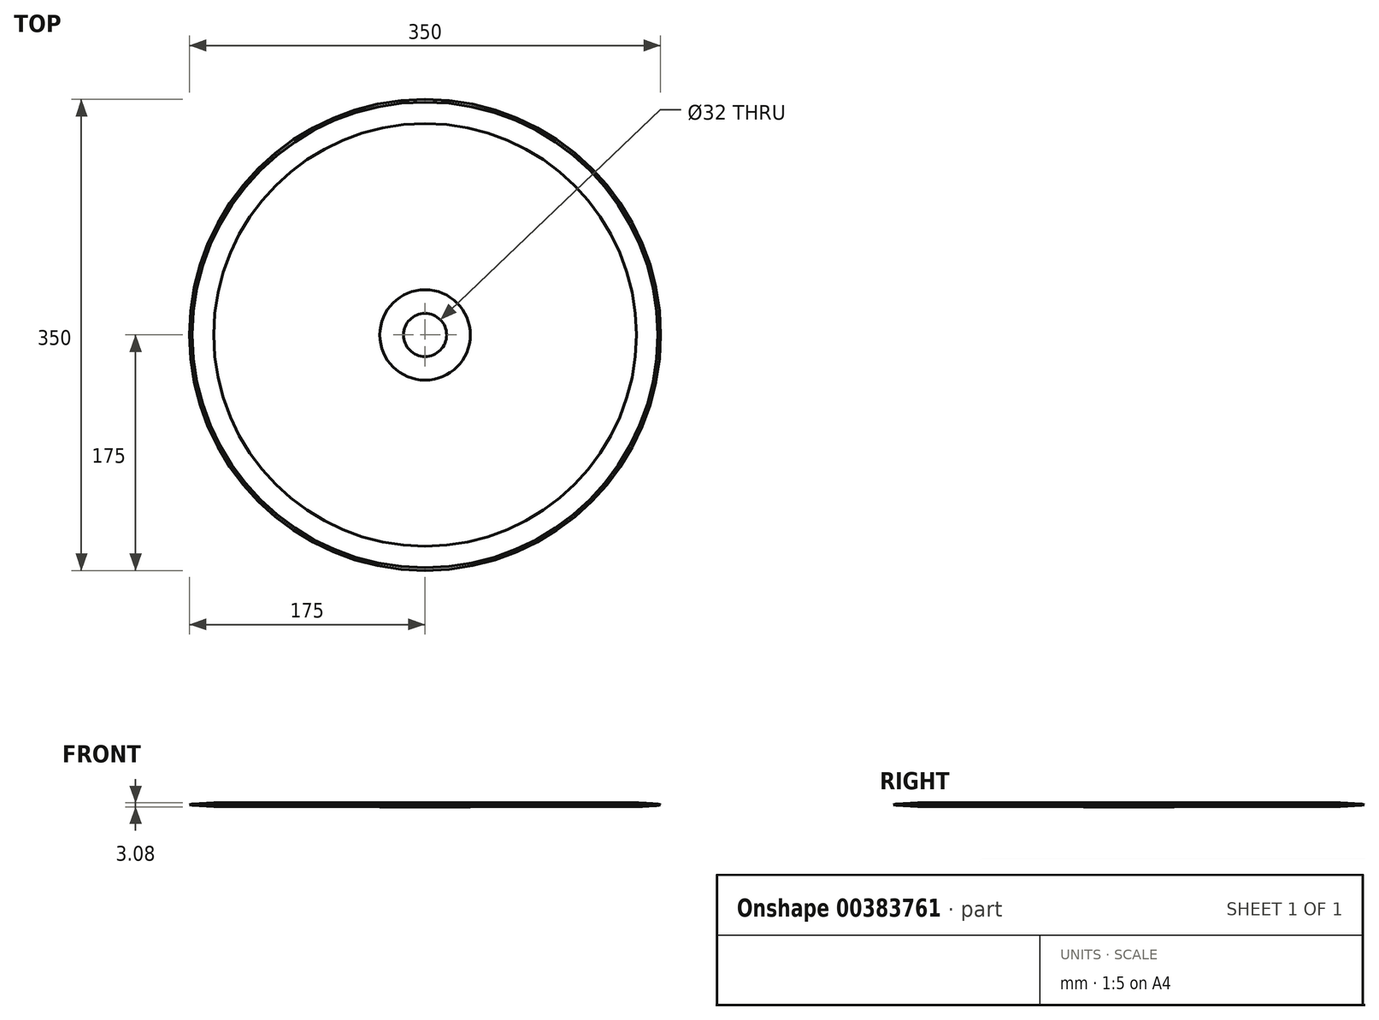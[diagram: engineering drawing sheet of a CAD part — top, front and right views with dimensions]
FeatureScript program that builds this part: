
annotation { "Feature Type Name" : "Feature", "Feature Type Description" : "" }
export const myFeature = defineFeature(function(context is Context, id is Id, definition is map)
    precondition{}
    {
        {
            var Q0;
            Q0=qCreatedBy(makeId("Front.planeOp"),FACE);
            var sketch = newSketch(context, id + "F0", { "sketchPlane" : qUnion([Q0])});
            skLineSegment(sketch, "E0", {"start": v(16, 1.54) * mm, "end": v(33.6, 1.54) * mm});
            skLineSegment(sketch, "E1", {"start": v(33.6, 1.54) * mm, "end": v(33.6, 1.45) * mm});
            skLineSegment(sketch, "E2", {"start": v(16, 1.54) * mm, "end": v(16, 0) * mm});
            skLineSegment(sketch, "E3", {"start": v(33.6, 1.45) * mm, "end": v(157, 1.45) * mm});
            skLineSegment(sketch, "E4", {"start": v(173, 0.5) * mm, "end": v(157, 1.45) * mm});
            skLineSegment(sketch, "E5", {"start": v(175, 0) * mm, "end": v(173, 0.5) * mm});
            skLineSegment(sketch, "E6", {"start": v(0, 0) * mm, "end": v(175, 0) * mm, "construction": true});
            skLineSegment(sketch, "E7.MirrorCS", {"start": v(33.6, -1.54) * mm, "end": v(33.6, -1.45) * mm});
            skLineSegment(sketch, "E8.MirrorCS", {"start": v(175, 0) * mm, "end": v(173, -0.5) * mm});
            skLineSegment(sketch, "E9.MirrorCS", {"start": v(16, -1.54) * mm, "end": v(16, 0) * mm});
            skLineSegment(sketch, "E10.MirrorCS", {"start": v(16, -1.54) * mm, "end": v(33.6, -1.54) * mm});
            skLineSegment(sketch, "E11.MirrorCS", {"start": v(173, -0.5) * mm, "end": v(157, -1.45) * mm});
            skLineSegment(sketch, "E12.MirrorCS", {"start": v(33.6, -1.45) * mm, "end": v(157, -1.45) * mm});
            skSolve(sketch);
        }
        {
            var Q0;
            Q0=qCreatedBy(makeId("Front.planeOp"),FACE);
            var sketch = newSketch(context, id + "F1", { "sketchPlane" : qUnion([Q0])});
            skLineSegment(sketch, "E13", {"start": v(0, 0) * mm, "end": v(0, 20.5) * mm, "construction": true});
            skSolve(sketch);
        }
        {
            var Q0;
            Q0=sQuery(id+"F1.wireOp",EDGE,"E13");
            var Q1;
            Q1=sQuery(id+"F0.wireOp",EDGE,"E9.MirrorCS");
            var Q2;
            Q2=sQuery(id+"F0.wireOp",EDGE,"E11.MirrorCS");
            var Q3;
            Q3=sQuery(id+"F0.wireOp",EDGE,"E12.MirrorCS");
            var Q4;
            Q4=sQuery(id+"F0.wireOp",EDGE,"E10.MirrorCS");
            var Q5;
            Q5=sQuery(id+"F0.wireOp",EDGE,"E4");
            var Q6;
            Q6=sQuery(id+"F0.wireOp",EDGE,"E3");
            var Q7;
            Q7=sQuery(id+"F0.wireOp",EDGE,"E0");
            var Q8;
            Q8=sQuery(id+"F0.wireOp",EDGE,"E8.MirrorCS");
            var Q9;
            Q9=sQuery(id+"F0.wireOp",EDGE,"E5");
            var Q10;
            Q10=sQuery(id+"F0.wireOp",EDGE,"E2");
            var Q11;
            Q11=sQuery(id+"F0.wireOp",EDGE,"E1");
            var Q12;
            Q12=sQuery(id+"F0.wireOp",EDGE,"E7.MirrorCS");
            var Q13;
            Q13=sQuery(id+"F1.wireOp",EDGE,"E13");
            revolve(context, id + "F2", {"bodyType" : ToolBodyType.SURFACE, "surfaceEntities" : qUnion([Q0, Q1, Q2, Q3, Q4, Q5, Q6, Q7, Q8, Q9, Q10, Q11, Q12]), "axis" : qUnion([Q13]), "revolveType" : RevolveType.FULL});
        }
    });
